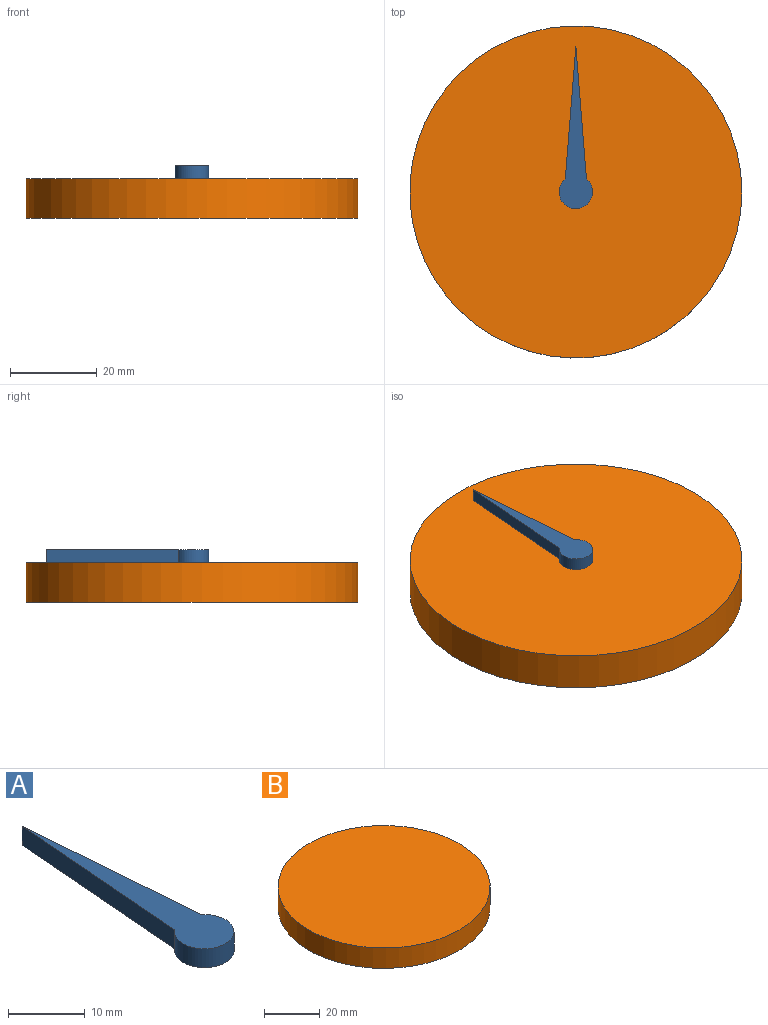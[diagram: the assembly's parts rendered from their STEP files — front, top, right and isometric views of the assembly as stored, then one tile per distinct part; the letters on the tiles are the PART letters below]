
ASSEMBLY  parts=2 mates=1
PART A: 5 faces, bbox 7.7x37.4x3 mm
  f0: cylinder r=3.86mm len=7.71mm, axis (0,0,-1), area 56.9mm2, adj f1,f2,f3,f4
  f1: plane 30.51x3mm, normal (1,0.08,0), area 91.8mm2, adj f0,f2,f3,f4
  f2: plane 30.5x3mm, normal (-1,0.08,0), area 91.8mm2, adj f0,f1,f3,f4
  f3: plane 37.36x7.71mm, normal (0,0,1), area 117.9mm2, adj f0,f1,f2
  f4: plane 37.36x7.71mm, normal (0,0,-1), area 117.9mm2, adj f0,f1,f2
PART B: 3 faces, bbox 76.4x76.4x9 mm
  f0: cylinder r=38.2mm len=76.41mm, axis (0,0,-1), area 2160.3mm2, adj f1,f2
  f1: plane 76.41x76.41mm, normal (0,0,1), area 4585.1mm2, adj f0
  f2: plane 76.41x76.41mm, normal (0,0,-1), area 4585.1mm2, adj f0
PLACE A at identity
PLACE B at identity fixed
MATE revolute B.f0 <-> A.f0  axis (0,0,1) through (0,0,9)mm
